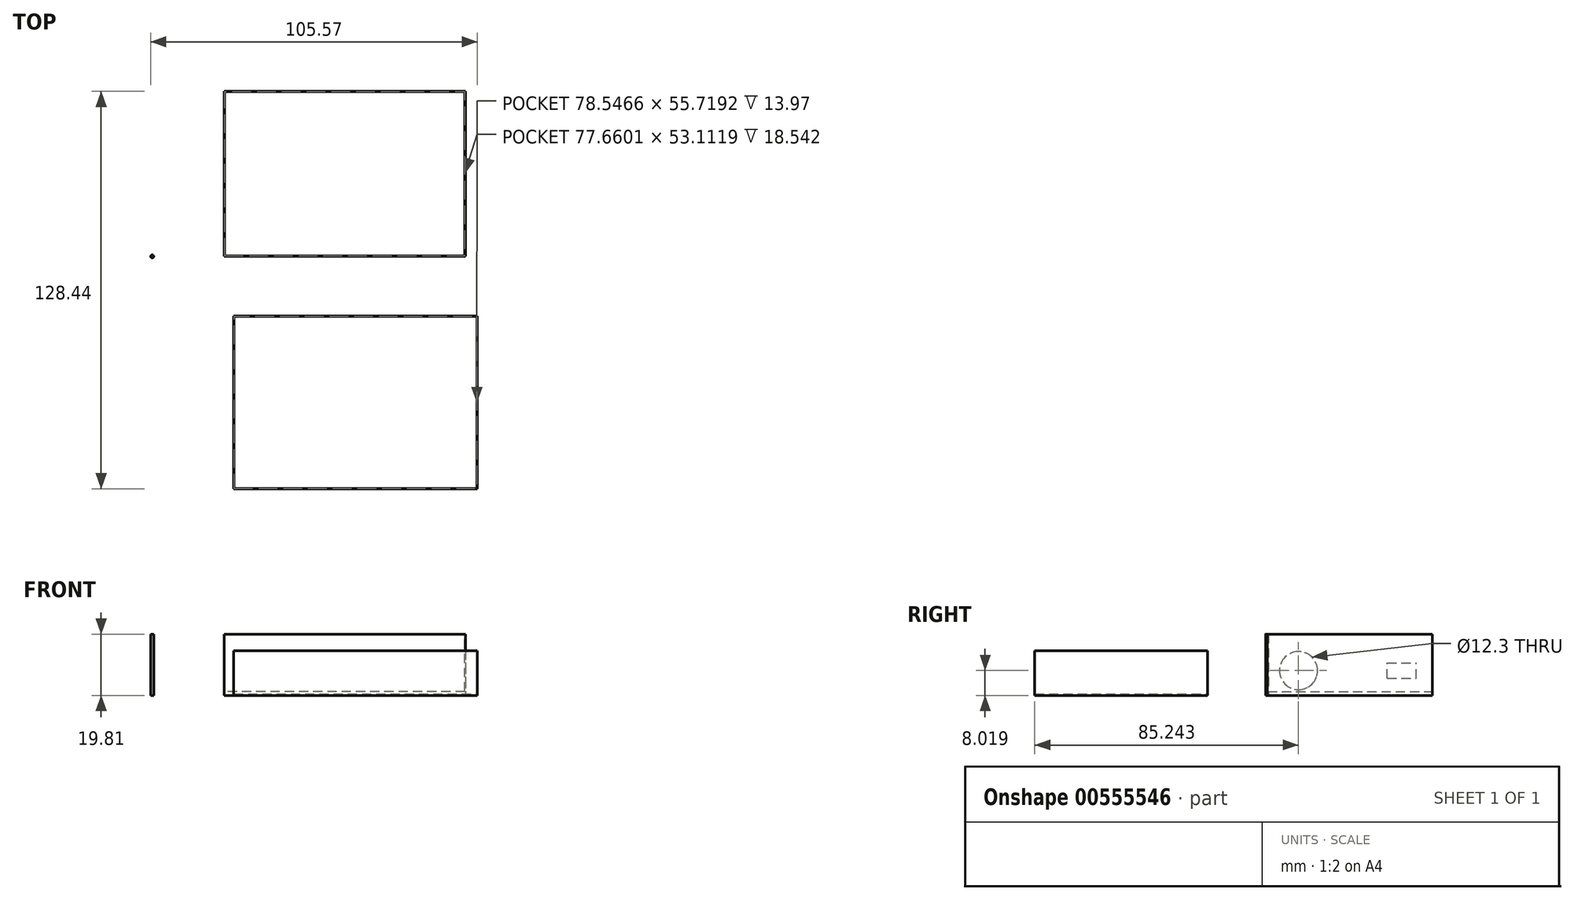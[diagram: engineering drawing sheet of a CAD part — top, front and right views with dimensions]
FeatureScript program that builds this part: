
annotation { "Feature Type Name" : "Feature", "Feature Type Description" : "" }
export const myFeature = defineFeature(function(context is Context, id is Id, definition is map)
    precondition{}
    {
        {
            var Q0;
            Q0=qCreatedBy(makeId("Top.planeOp"),FACE);
            var sketch = newSketch(context, id + "F0", { "sketchPlane" : qUnion([Q0])});
            skCircle(sketch, "E0", {"center": v(-101.26, 0) * mm, "radius": 0.48 * mm});
            skLineSegment(sketch, "E1.bottom", {"start": v(0, 0) * mm, "end": v(-77.98, 0) * mm});
            skLineSegment(sketch, "E1.top", {"start": v(0, 53.34) * mm, "end": v(-77.98, 53.34) * mm});
            skLineSegment(sketch, "E1.left", {"start": v(0, 0) * mm, "end": v(0, 53.34) * mm});
            skLineSegment(sketch, "E1.right", {"start": v(-77.98, 0) * mm, "end": v(-77.98, 53.34) * mm});
            skSolve(sketch);
        }
        {
            var Q0;
            Q0 = qSketchRegion(id + "F0", true);
            extrude(context, id + "F1", {"entities" : qUnion([Q0]), "depth" : 19.8 * mm, "offsetDistance" : 25.4 * mm});
        }
        {
            var Q0;
            Q0=makeQuery(id+"F1.opExtrude","SWEPT_FACE",FACE,{"disambiguationData":[OSD([sQuery(id+"F0.wireOp",EDGE,"E1.right")])]});
            var sketch = newSketch(context, id + "F2", { "sketchPlane" : qUnion([Q0])});
            skCircle(sketch, "E2", {"center": v(-10.14, 8.02) * mm, "radius": 6.15 * mm});
            skSolve(sketch);
        }
        {
            var Q0;
            Q0=makeQuery(id+"F2.imprint","IMPRINT",FACE,{"disambiguationData":[TD([[makeQuery(id+"F2.imprint","IMPRINT",EDGE,{"derivedFrom":sQuery(id+"F2.wireOp",EDGE,"E2")}),1.0]])]});
            extrude(context, id + "F3", {"entities" : qUnion([Q0]), "operationType" : NewBodyOperationType.REMOVE, "oppositeDirection" : true, "depth" : 25.4 * mm, "offsetDistance" : 25.4 * mm});
        }
        {
            var Q0;
            Q0=makeQuery(id+"F1.opExtrude","CAP_FACE",FACE,{"disambiguationData":[OSD([sQuery(id+"F0.wireOp",EDGE,"E1.bottom"),sQuery(id+"F0.wireOp",EDGE,"E1.top"),sQuery(id+"F0.wireOp",EDGE,"E1.left"),sQuery(id+"F0.wireOp",EDGE,"E1.right")])],"isStart":false});
            var sketch = newSketch(context, id + "F4", { "sketchPlane" : qUnion([Q0])});
            skLineSegment(sketch, "E3.bottom", {"start": v(-0.25, 0.17) * mm, "end": v(-77.9, 0.17) * mm});
            skLineSegment(sketch, "E3.top", {"start": v(-0.25, 53.28) * mm, "end": v(-77.9, 53.28) * mm});
            skLineSegment(sketch, "E3.left", {"start": v(-0.25, 0.17) * mm, "end": v(-0.25, 53.28) * mm});
            skLineSegment(sketch, "E3.right", {"start": v(-77.9, 0.17) * mm, "end": v(-77.9, 53.28) * mm});
            skSolve(sketch);
        }
        {
            var Q0;
            Q0 = qSketchRegion(id + "F4", true);
            extrude(context, id + "F5", {"entities" : qUnion([Q0]), "operationType" : NewBodyOperationType.REMOVE, "oppositeDirection" : true, "depth" : 18.54 * mm, "offsetDistance" : 25.4 * mm});
        }
        {
            var Q0;
            Q0=makeQuery(id+"F1.opExtrude","SWEPT_FACE",FACE,{"disambiguationData":[OSD([sQuery(id+"F0.wireOp",EDGE,"E1.right")])]});
            var sketch = newSketch(context, id + "F6", { "sketchPlane" : qUnion([Q0])});
            skLineSegment(sketch, "E4.bottom", {"start": v(-38.78, 5.5) * mm, "end": v(-48.2, 5.5) * mm});
            skLineSegment(sketch, "E4.top", {"start": v(-38.78, 10.49) * mm, "end": v(-48.2, 10.49) * mm});
            skLineSegment(sketch, "E4.left", {"start": v(-38.78, 5.5) * mm, "end": v(-38.78, 10.49) * mm});
            skLineSegment(sketch, "E4.right", {"start": v(-48.2, 5.5) * mm, "end": v(-48.2, 10.49) * mm});
            skSolve(sketch);
        }
        {
            var Q0;
            Q0 = qSketchRegion(id + "F6", true);
            extrude(context, id + "F7", {"entities" : qUnion([Q0]), "operationType" : NewBodyOperationType.REMOVE, "oppositeDirection" : true, "depth" : 25.4 * mm, "offsetDistance" : 25.4 * mm});
        }
        {
            var Q0;
            Q0=qCreatedBy(makeId("Top.planeOp"),FACE);
            var sketch = newSketch(context, id + "F8", { "sketchPlane" : qUnion([Q0])});
            skLineSegment(sketch, "E5.bottom", {"start": v(3.83, -19.22) * mm, "end": v(-74.91, -19.22) * mm});
            skLineSegment(sketch, "E5.top", {"start": v(3.83, -75.1) * mm, "end": v(-74.91, -75.1) * mm});
            skLineSegment(sketch, "E5.left", {"start": v(3.83, -19.22) * mm, "end": v(3.83, -75.1) * mm});
            skLineSegment(sketch, "E5.right", {"start": v(-74.91, -19.22) * mm, "end": v(-74.91, -75.1) * mm});
            skSolve(sketch);
        }
        {
            var Q0;
            Q0 = qSketchRegion(id + "F8", true);
            extrude(context, id + "F9", {"entities" : qUnion([Q0]), "depth" : 14.48 * mm, "offsetDistance" : 25.4 * mm});
        }
        {
            var Q0;
            Q0=makeQuery(id+"F9.opExtrude","CAP_FACE",FACE,{"disambiguationData":[OSD([sQuery(id+"F8.wireOp",EDGE,"E5.bottom"),sQuery(id+"F8.wireOp",EDGE,"E5.top"),sQuery(id+"F8.wireOp",EDGE,"E5.left"),sQuery(id+"F8.wireOp",EDGE,"E5.right")])],"isStart":false});
            var sketch = newSketch(context, id + "F10", { "sketchPlane" : qUnion([Q0])});
            skLineSegment(sketch, "E6.bottom", {"start": v(-74.87, -75.07) * mm, "end": v(3.67, -75.07) * mm});
            skLineSegment(sketch, "E6.top", {"start": v(-74.87, -19.35) * mm, "end": v(3.67, -19.35) * mm});
            skLineSegment(sketch, "E6.left", {"start": v(-74.87, -75.07) * mm, "end": v(-74.87, -19.35) * mm});
            skLineSegment(sketch, "E6.right", {"start": v(3.67, -75.07) * mm, "end": v(3.67, -19.35) * mm});
            skSolve(sketch);
        }
        {
            var Q0;
            Q0 = qSketchRegion(id + "F10", true);
            extrude(context, id + "F11", {"entities" : qUnion([Q0]), "operationType" : NewBodyOperationType.REMOVE, "oppositeDirection" : true, "depth" : 13.97 * mm, "offsetDistance" : 25.4 * mm});
        }
    });
